annotation { "Feature Type Name" : "Feature", "Feature Type Description" : "" }
export const myFeature = defineFeature(function(context is Context, id is Id, definition is map)
    precondition{}
    {
        {
            var Q0;
            Q0=qCreatedBy(makeId("Top.planeOp"),FACE);
            var sketch = newSketch(context, id + "F0", { "sketchPlane" : qUnion([Q0])});
            skArc(sketch, "E0", {"start": v(-6.77, 15) * mm, "mid": v(-40, 0) * mm, "end": v(-6.77, -15) * mm});
            skArc(sketch, "E1", {"start": v(15, -12.5) * mm, "mid": v(27.5, 0) * mm, "end": v(15, 12.5) * mm});
            skLineSegment(sketch, "E2", {"start": v(15, 12.5) * mm, "end": v(-0.16, 12.5) * mm});
            skLineSegment(sketch, "E3", {"start": v(15, -12.5) * mm, "end": v(-0.16, -12.5) * mm});
            skPoint(sketch, "E4.visualSharp", {"position": v(-4.39, 12.5) * mm});
            skArc(sketch, "E4.filletArc", {"start": v(-6.77, 15) * mm, "mid": v(-3.7, 13.15) * mm, "end": v(-0.16, 12.5) * mm});
            skPoint(sketch, "E5.visualSharp", {"position": v(-4.39, -12.5) * mm});
            skArc(sketch, "E5.filletArc", {"start": v(-0.16, -12.5) * mm, "mid": v(-3.7, -13.15) * mm, "end": v(-6.77, -15) * mm});
            skSolve(sketch);
        }
        {
            var Q0;
            Q0=qSketchRegion(id+"F0",true);
            extrude(context, id + "F1", {"entities" : qUnion([Q0]), "depth" : 15 * mm, "hasDraft" : true, "draftAngle" : 25 * degree});
        }
        {
            var Q0;
            Q0=makeQuery(id+"F1.opExtrude","CAP_FACE",FACE,{"disambiguationData":[OSD([sQuery(id+"F0.wireOp",EDGE,"E0"),sQuery(id+"F0.wireOp",EDGE,"E1"),sQuery(id+"F0.wireOp",EDGE,"E2"),sQuery(id+"F0.wireOp",EDGE,"E3"),sQuery(id+"F0.wireOp",EDGE,"E4.filletArc"),sQuery(id+"F0.wireOp",EDGE,"E5.filletArc")])],"isStart":false});
            shell(context, id + "F2", {"entities" : qUnion([Q0]), "thickness" : 2 * mm});
        }
        {
            var Q0;
            Q0=makeQuery(id+"F2.opShell","OFFSET_FACE",FACE,{"disambiguationData":[OSD([sQuery(id+"F0.wireOp",EDGE,"E0"),sQuery(id+"F0.wireOp",EDGE,"E1"),sQuery(id+"F0.wireOp",EDGE,"E2"),sQuery(id+"F0.wireOp",EDGE,"E3"),sQuery(id+"F0.wireOp",EDGE,"E4.filletArc"),sQuery(id+"F0.wireOp",EDGE,"E5.filletArc")])]});
            var sketch = newSketch(context, id + "F3", { "sketchPlane" : qUnion([Q0])});
            skText(sketch, "E6", { "text": "Merlin Thoune\n", "fontName": "OpenSans-Regular.ttf"});
            const initialGuessF3  = {"E6": [-0.033, -0.00287, 1, 0, 0.0058]};
            skSetInitialGuess(sketch, initialGuessF3);
            skSolve(sketch);
        }
        {
            var Q0;
            Q0 = qSketchRegion(id + "F3", true);
            extrude(context, id + "F4", {"entities" : qUnion([Q0]), "operationType" : NewBodyOperationType.ADD, "depth" : 5.8 * mm});
        }
    });